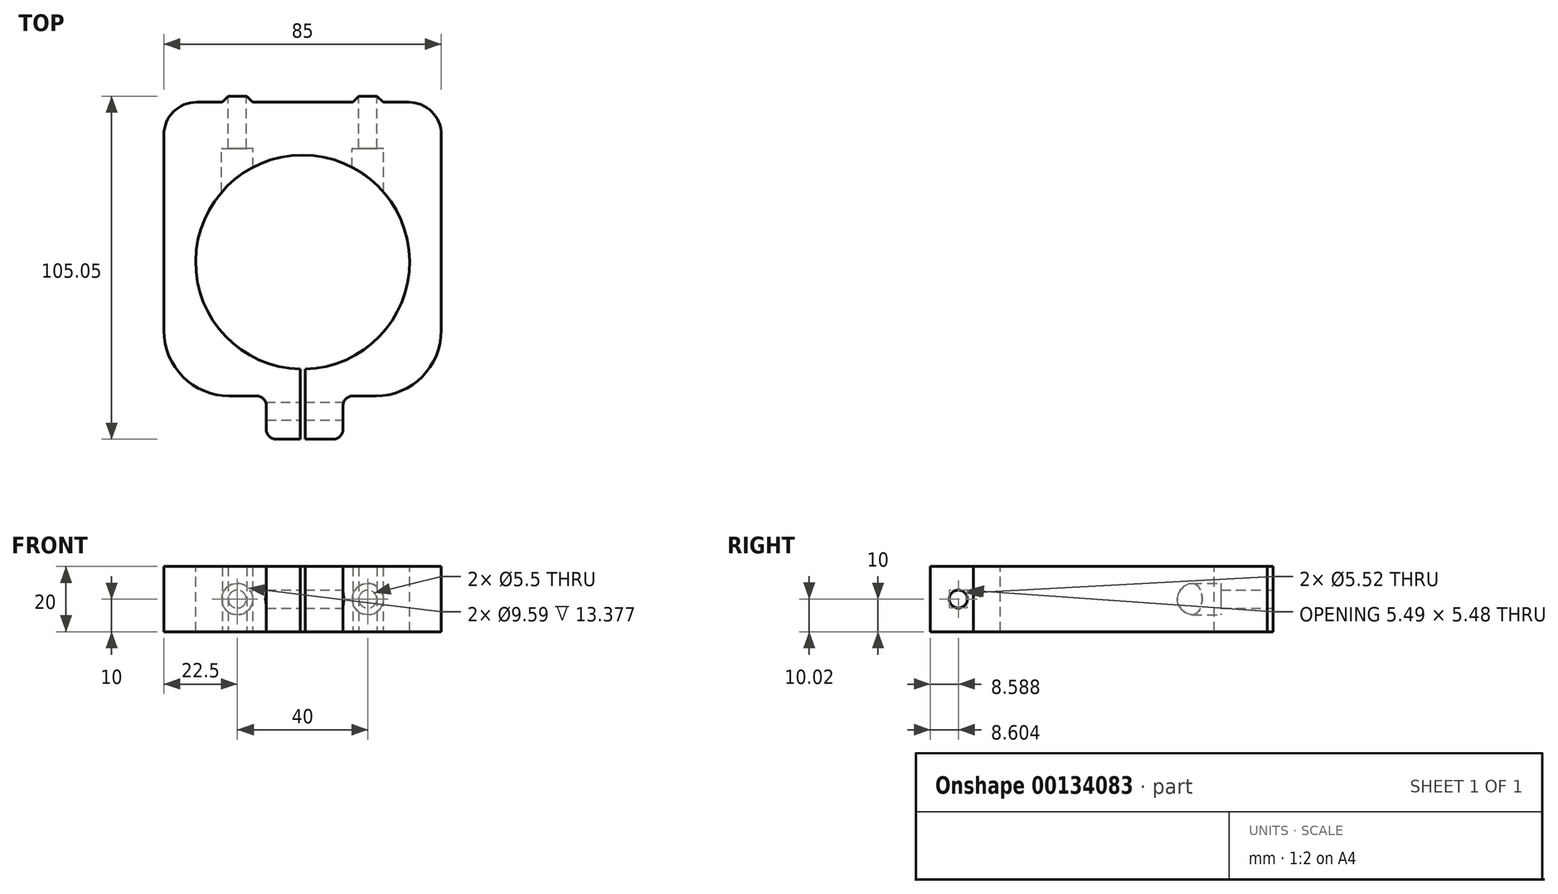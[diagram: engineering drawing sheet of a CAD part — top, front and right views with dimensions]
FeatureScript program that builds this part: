
annotation { "Feature Type Name" : "Feature", "Feature Type Description" : "" }
export const myFeature = defineFeature(function(context is Context, id is Id, definition is map)
    precondition{}
    {
        {
            var Q0;
            Q0=qCreatedBy(makeId("Top.planeOp"),FACE);
            var sketch = newSketch(context, id + "F0", { "sketchPlane" : qUnion([Q0])});
            skLineSegment(sketch, "E0", {"start": v(-32.5, 44.15) * mm, "end": v(0, 44.15) * mm});
            skLineSegment(sketch, "E1", {"start": v(0, 44.15) * mm, "end": v(32.5, 44.15) * mm});
            skLineSegment(sketch, "E2", {"start": v(42.5, 34.15) * mm, "end": v(42.5, 0) * mm});
            skLineSegment(sketch, "E3", {"start": v(42.5, 0) * mm, "end": v(42.5, -25.85) * mm});
            skLineSegment(sketch, "E4", {"start": v(22.5, -45.85) * mm, "end": v(15.4, -45.85) * mm});
            skLineSegment(sketch, "E5", {"start": v(12.4, -48.85) * mm, "end": v(12.4, -56.1) * mm});
            skLineSegment(sketch, "E6", {"start": v(9.4, -59.1) * mm, "end": v(-8.13, -59.1) * mm});
            skLineSegment(sketch, "E7", {"start": v(-11.13, -56.1) * mm, "end": v(-11.13, -48.85) * mm});
            skLineSegment(sketch, "E8", {"start": v(-14.13, -45.85) * mm, "end": v(-22.5, -45.85) * mm});
            skLineSegment(sketch, "E9", {"start": v(-42.5, -25.85) * mm, "end": v(-42.5, 0) * mm});
            skLineSegment(sketch, "E10", {"start": v(-42.5, 0) * mm, "end": v(-42.5, 34.15) * mm});
            skLineSegment(sketch, "E11", {"start": v(-42.5, 0) * mm, "end": v(0, 0) * mm, "construction": true});
            skLineSegment(sketch, "E12", {"start": v(0, 0) * mm, "end": v(42.5, 0) * mm, "construction": true});
            skPoint(sketch, "E13.visualSharp", {"position": v(-42.5, 44.15) * mm});
            skArc(sketch, "E13.filletArc", {"start": v(-32.5, 44.15) * mm, "mid": v(-39.57, 41.22) * mm, "end": v(-42.5, 34.15) * mm});
            skPoint(sketch, "E14.visualSharp", {"position": v(42.5, 44.15) * mm});
            skArc(sketch, "E14.filletArc", {"start": v(42.5, 34.15) * mm, "mid": v(39.57, 41.22) * mm, "end": v(32.5, 44.15) * mm});
            skPoint(sketch, "E15.visualSharp", {"position": v(-42.5, -45.85) * mm});
            skArc(sketch, "E15.filletArc", {"start": v(-42.5, -25.85) * mm, "mid": v(-36.64, -40) * mm, "end": v(-22.5, -45.85) * mm});
            skPoint(sketch, "E16.visualSharp", {"position": v(-11.13, -45.85) * mm});
            skArc(sketch, "E16.filletArc", {"start": v(-11.13, -48.85) * mm, "mid": v(-12, -46.73) * mm, "end": v(-14.13, -45.85) * mm});
            skPoint(sketch, "E17.visualSharp", {"position": v(12.4, -45.85) * mm});
            skArc(sketch, "E17.filletArc", {"start": v(15.4, -45.85) * mm, "mid": v(13.29, -46.73) * mm, "end": v(12.4, -48.85) * mm});
            skPoint(sketch, "E18.visualSharp", {"position": v(12.4, -59.1) * mm});
            skArc(sketch, "E18.filletArc", {"start": v(9.4, -59.1) * mm, "mid": v(11.53, -58.22) * mm, "end": v(12.4, -56.1) * mm});
            skPoint(sketch, "E19.visualSharp", {"position": v(-11.13, -59.1) * mm});
            skArc(sketch, "E19.filletArc", {"start": v(-11.13, -56.1) * mm, "mid": v(-10.25, -58.22) * mm, "end": v(-8.13, -59.1) * mm});
            skPoint(sketch, "E20.visualSharp", {"position": v(42.5, -45.85) * mm});
            skArc(sketch, "E20.filletArc", {"start": v(22.5, -45.85) * mm, "mid": v(36.64, -40) * mm, "end": v(42.5, -25.85) * mm});
            skLineSegment(sketch, "E21", {"start": v(-42.5, 44.15) * mm, "end": v(-20, 44.15) * mm, "construction": true});
            skLineSegment(sketch, "E22", {"start": v(-20, 44.15) * mm, "end": v(20, 44.15) * mm, "construction": true});
            skLineSegment(sketch, "E23", {"start": v(20, 44.15) * mm, "end": v(42.5, 44.15) * mm, "construction": true});
            skLineSegment(sketch, "E24", {"start": v(-20, 44.15) * mm, "end": v(-20, 45.95) * mm});
            skLineSegment(sketch, "E25", {"start": v(-20, 45.95) * mm, "end": v(-22.84, 45.95) * mm});
            skLineSegment(sketch, "E26", {"start": v(-20, 45.95) * mm, "end": v(-17.16, 45.95) * mm});
            skLineSegment(sketch, "E27", {"start": v(-27.4, 41.38) * mm, "end": v(-20, 48.79) * mm, "construction": true});
            skLineSegment(sketch, "E28", {"start": v(-20, 48.79) * mm, "end": v(-12.6, 41.38) * mm, "construction": true});
            skLineSegment(sketch, "E29", {"start": v(-20, 45.95) * mm, "end": v(-20, 52.75) * mm, "construction": true});
            skLineSegment(sketch, "E30", {"start": v(-24.64, 44.15) * mm, "end": v(-22.84, 45.95) * mm});
            skLineSegment(sketch, "E31", {"start": v(-17.16, 45.95) * mm, "end": v(-15.36, 44.15) * mm});
            skLineSegment(sketch, "E32", {"start": v(20, 44.15) * mm, "end": v(20, 45.95) * mm, "construction": true});
            skLineSegment(sketch, "E33", {"start": v(20, 45.95) * mm, "end": v(20, 53.01) * mm, "construction": true});
            skLineSegment(sketch, "E34", {"start": v(20, 45.95) * mm, "end": v(22.84, 45.95) * mm});
            skLineSegment(sketch, "E35", {"start": v(20, 45.95) * mm, "end": v(17.16, 45.95) * mm});
            skLineSegment(sketch, "E36", {"start": v(12.51, 41.3) * mm, "end": v(20, 48.79) * mm, "construction": true});
            skLineSegment(sketch, "E37", {"start": v(20, 48.79) * mm, "end": v(27.49, 41.3) * mm, "construction": true});
            skLineSegment(sketch, "E38", {"start": v(15.36, 44.15) * mm, "end": v(17.16, 45.95) * mm});
            skLineSegment(sketch, "E39", {"start": v(22.84, 45.95) * mm, "end": v(24.64, 44.15) * mm});
            skLineSegment(sketch, "E40", {"start": v(-42.5, 44.15) * mm, "end": v(-42.5, -45.85) * mm, "construction": true});
            skSolve(sketch);
        }
        {
            var Q0;
            Q0=qSketchRegion(id+"F0",true);
            extrude(context, id + "F1", {"entities" : qUnion([Q0]), "endBound" : BoundingType.SYMMETRIC, "depth" : 20 * mm});
        }
        {
            var Q0;
            Q0=qCreatedBy(makeId("Top.planeOp"),FACE);
            var sketch = newSketch(context, id + "F2", { "sketchPlane" : qUnion([Q0])});
            skCircle(sketch, "E41", {"center": v(0, -4.85) * mm, "radius": 32.77 * mm});
            skLineSegment(sketch, "E42", {"start": v(0, 44.15) * mm, "end": v(0, -4.85) * mm, "construction": true});
            skSolve(sketch);
        }
        {
            var Q0;
            Q0=qSketchRegion(id+"F2",true);
            extrude(context, id + "F3", {"entities" : qUnion([Q0]), "operationType" : NewBodyOperationType.REMOVE, "endBound" : BoundingType.SYMMETRIC, "oppositeDirection" : true, "depth" : 20 * mm});
        }
        {
            var Q0;
            Q0=qCreatedBy(makeId("Top.planeOp"),FACE);
            var sketch = newSketch(context, id + "F4", { "sketchPlane" : qUnion([Q0])});
            skLineSegment(sketch, "E43.bottom", {"start": v(0, 0) * mm, "end": v(0.75, 0) * mm});
            skLineSegment(sketch, "E43.top", {"start": v(0, -80) * mm, "end": v(0.75, -80) * mm});
            skLineSegment(sketch, "E43.left", {"start": v(0, 0) * mm, "end": v(0, -80) * mm});
            skLineSegment(sketch, "E43.right", {"start": v(0.75, 0) * mm, "end": v(0.75, -80) * mm});
            skLineSegment(sketch, "E44.bottom", {"start": v(0, 0) * mm, "end": v(-0.75, 0) * mm});
            skLineSegment(sketch, "E44.top", {"start": v(0, -80) * mm, "end": v(-0.75, -80) * mm});
            skLineSegment(sketch, "E44.right", {"start": v(-0.75, 0) * mm, "end": v(-0.75, -80) * mm});
            skSolve(sketch);
        }
        {
            var Q0;
            Q0=qSketchRegion(id+"F4",true);
            extrude(context, id + "F5", {"entities" : qUnion([Q0]), "operationType" : NewBodyOperationType.REMOVE, "endBound" : BoundingType.SYMMETRIC, "oppositeDirection" : true, "depth" : 20 * mm});
        }
        {
            var Q0;
            Q0=qCreatedBy(makeId("Right.planeOp"),FACE);
            var sketch = newSketch(context, id + "F6", { "sketchPlane" : qUnion([Q0])});
            skLineSegment(sketch, "E45", {"start": v(-45.5, 0) * mm, "end": v(-50.51, 0) * mm, "construction": true});
            skLineSegment(sketch, "E46", {"start": v(-50.51, 0) * mm, "end": v(-55.52, 0) * mm, "construction": true});
            skLineSegment(sketch, "E47", {"start": v(-50.51, 0) * mm, "end": v(-50.51, -7.5) * mm, "construction": true});
            skLineSegment(sketch, "E48", {"start": v(-50.51, 0) * mm, "end": v(-50.51, 7.5) * mm, "construction": true});
            skCircle(sketch, "E49", {"center": v(-50.51, 0) * mm, "radius": 2.76 * mm});
            skSolve(sketch);
        }
        {
            var Q0;
            Q0=qSketchRegion(id+"F6",true);
            extrude(context, id + "F7", {"entities" : qUnion([Q0]), "operationType" : NewBodyOperationType.REMOVE, "endBound" : BoundingType.SYMMETRIC, "oppositeDirection" : true, "depth" : 50 * mm});
        }
        {
            var Q0;
            Q0=makeQuery(id+"F1.opExtrude","SWEPT_FACE",FACE,{"disambiguationData":[OSD([sQuery(id+"F0.wireOp",EDGE,"E0"),sQuery(id+"F0.wireOp",EDGE,"E1")])]});
            var sketch = newSketch(context, id + "F8", { "sketchPlane" : qUnion([Q0])});
            skLineSegment(sketch, "E50", {"start": v(0, 0) * mm, "end": v(20, 0) * mm, "construction": true});
            skLineSegment(sketch, "E51", {"start": v(0, 0) * mm, "end": v(-20, 0) * mm, "construction": true});
            skCircle(sketch, "E52", {"center": v(20, 0) * mm, "radius": 2.75 * mm});
            skCircle(sketch, "E53", {"center": v(-20, 0) * mm, "radius": 2.75 * mm});
            skSolve(sketch);
        }
        {
            var Q0;
            Q0=qSketchRegion(id+"F8",true);
            extrude(context, id + "F9", {"entities" : qUnion([Q0]), "operationType" : NewBodyOperationType.REMOVE, "endBound" : BoundingType.SYMMETRIC, "oppositeDirection" : true, "depth" : 35.8 * mm});
        }
        {
            var Q0;
            Q0=makeQuery(id+"F1.opExtrude","SWEPT_FACE",FACE,{"disambiguationData":[OSD([sQuery(id+"F0.wireOp",EDGE,"E0"),sQuery(id+"F0.wireOp",EDGE,"E1")])]});
            var sketch = newSketch(context, id + "F10", { "sketchPlane" : qUnion([Q0])});
            skCircle(sketch, "E54", {"center": v(20, 0) * mm, "radius": 4.8 * mm});
            skCircle(sketch, "E55", {"center": v(-20, 0) * mm, "radius": 4.8 * mm});
            skSolve(sketch);
        }
        {
            var Q0;
            Q0=qSketchRegion(id+"F10",true);
            extrude(context, id + "F11", {"entities" : qUnion([Q0]), "operationType" : NewBodyOperationType.REMOVE, "oppositeDirection" : true, "depth" : 29.9 * mm, "hasSecondDirection" : true, "secondDirectionOppositeDirection" : true, "secondDirectionDepth" : 14.2 * mm});
        }
    });
